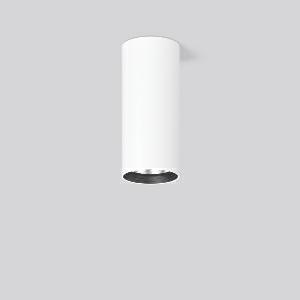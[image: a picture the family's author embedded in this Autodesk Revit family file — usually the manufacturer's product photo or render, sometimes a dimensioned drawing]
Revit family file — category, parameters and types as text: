
# Revit family: heledon_mini_a_931210_002_1_4b61
name_source: partatom
category: Lighting Fixtures
units: mm (PartAtom-declared; Revit-internal decimal feet)

## family parameters
Cut with Voids When Loaded = No
Host = Face
Light Source = No
Part Type = Normal
Room Calculation Point = No
Round Connector Dimension = Use Diameter
Shared = No

## types (1)
- HELEDON mini A (1 x LED Modul 940, 3900 lm, 4000)
    Apparent Load = 29 VA
    Approval mark = CE
    CIE Flux Codes = 95 99 100 100 100
    Color Rendering = 92
    Color Temperature = 4000
    Default Elevation = 1800 mm
    Description = Series: HELEDON mini
Cylindrical surface-mounted downlight. Housing: die-cast aluminium, powder-coated. Internal ceiling frame polycarbonate with bayonet mounting. Black plastic ring and recessed LED to prevent glare from the side. Optical assembly with reflector made of MIRO-Silver with 98% total light reflection for outstanding efficiency - can be changed without tools. Best colour rendering index Ra>90. Suitable for Ceiling mounting. Easy installation with a separate ceiling frame with bayonet mounting and plug connection. Driver integrated. Connected via plug-in connector. High quality converter without flickering and stroboscopic effect. The following accessories can be mounted without use of tools: interchangeable lenses, decorative glasses, honeycomb louvre, clear and frosted diffusers, white interchangeable plastic ring. 
Colour: traffic white, matt (RAL 9016)
Diameter: 87 mm
Height: 197 mm
Lamp: LED
Socket: without socket
Colour temperature: 4000K
Colour rendering index (CRI): 92
System power: 29 W
Rated luminous flux: 3900 lm
Luminous efficiency: 134 lm/W
Control gear: Regulated power supply
Protection class: I
Type of protection: IP 20
    Height = 197 mm
    Lamp = 1 x LED Modul 940
    Lamp Light Flux = 3900 lm
    Lamp count = 1
    Length = 87 mm
    Lifetime = 50000 h
    Luminous efficacy = 134 lm/W
    Manufacturer = RZB
    ModVariant = No
    Model = 931210.002.1
    Mounting Place = Ceiling
    Mounting Type = Surface mounted
    Number of Poles = 1
    OnlyDefault = Yes
    Power Factor = 1
    Product Name = HELEDON mini A
    Product group = Surface mounted downlights
    ProductGroupID = 302
    Protection Class = Protection class I
    Protection Degree = IP 20
    RLX_Detail_Level = 1
    RLX_Emergency_Light_Flux = 0 lm
    RLX_Emergency_Type = 0
    RLX_Emergency_Type_DB = No
    RlxData = <blob elided: 107173 chars, md5=32558f3f>
    Socket = socket
    Standby Power = 0 W
    System Light Flux = 3900 lm
    System Power = 29 W
    Type Comments = Product without accessories
    Type Image = 931188.002.jpg
    URL = http://relux.com
    VarID = ---
    Voltage = 230 V
    Voltage Range = 220-240 V
    Weight = 0.00 kg
    Width = 0 mm  [stored 0 ft]

note: [stored X ft] marks values corroborated as IEEE doubles in the binary element streams (Revit-internal decimal feet)

## geometry (parser evidence)
native form markers: Blend x4, Sweep x11
no freeform markers — native parametric forms only
